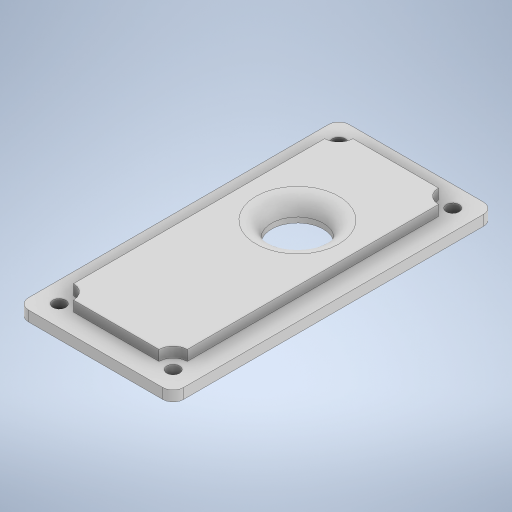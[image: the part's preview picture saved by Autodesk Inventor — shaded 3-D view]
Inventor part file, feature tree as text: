
AUTODESK INVENTOR PART (.ipt)
format: ipt  version: 2023.1 (Build 271208000, 208)  size: 288,256 bytes
history: native  units: mm
features: extrude x3, sketch x2, fillet x2, other x1
ambient origin geometry x8: Origin, YZ Plane, XZ Plane, XY Plane, X Axis, Y Axis, Z Axis, Center Point
bodies: Body1 (feature_tree)
feature tree (8):
  other  "솔리드1"
  sketch  "스케치1"
  extrude  "돌출1"  Depth=22.0mm
  extrude  "돌출2"  Depth=54.0mm
  fillet  "모깎기1"  Radius=4.0mm
  extrude  "돌출3"  Depth=2.5mm
  fillet  "모깎기2"  Radius=5.5mm
  sketch  "스케치2"
